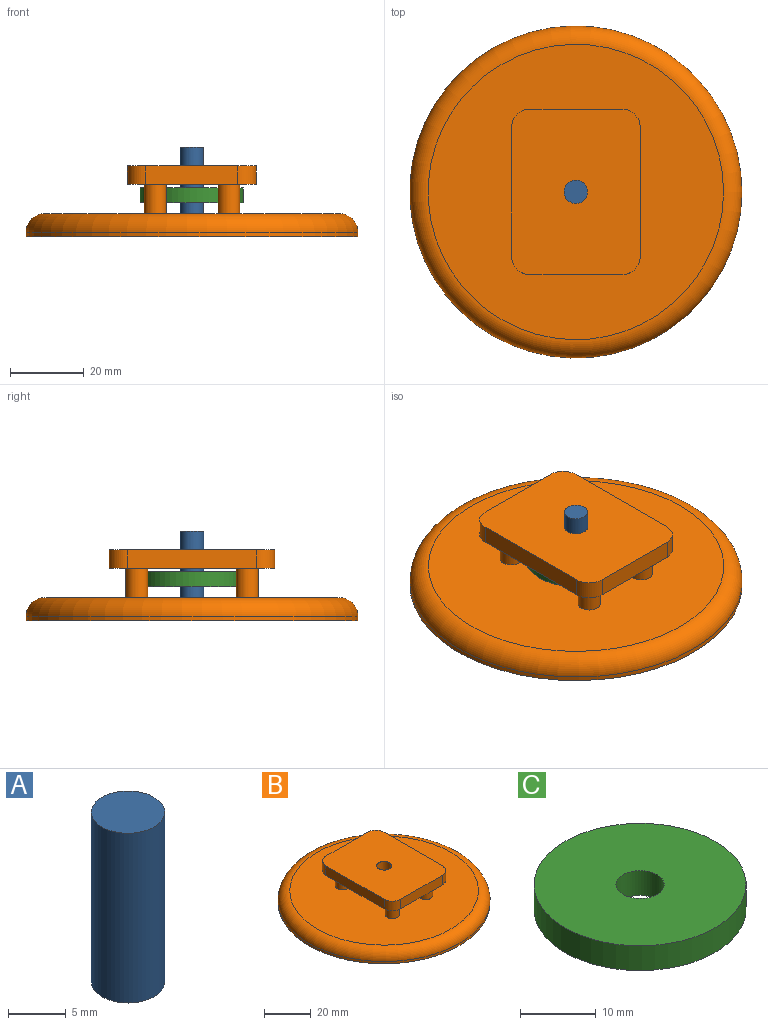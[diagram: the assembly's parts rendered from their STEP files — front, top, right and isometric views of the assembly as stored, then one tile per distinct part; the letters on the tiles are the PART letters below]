
ASSEMBLY  parts=3 mates=2
PART A: 3 faces, bbox 6.4x6.4x18 mm
  f0: cylinder r=3.17mm len=18mm, axis (0,0,-1), area 359.1mm2, adj f1,f2
  f1: plane 6.35x6.35mm, normal (0,0,-1), area 31.7mm2, adj f0
  f2: plane 6.35x6.35mm, normal (0,0,1), area 31.7mm2, adj f0
PART B: 19 faces, bbox 97.7x97.7x19.2 mm
  f0: cylinder r=45.15mm len=90.3mm, axis (0,0,-1), area 340.4mm2, adj f2,f3
  f1: plane 80.3x80.3mm, normal (0,0,1), area 4951.7mm2, adj f3,f4,f5,f6,f7
  f2: plane 90.3x90.3mm, normal (0,0,-1), area 6404.8mm2, adj f0
  f3: torus R=40.15mm, axis (0,0,1), area 2138.5mm2, adj f0,f1
  f4: cylinder r=3mm len=8mm, axis (0,0,-1), area 150.8mm2, adj f1,f14
  f5: cylinder r=3mm len=8mm, axis (0,0,-1), area 150.8mm2, adj f1,f14
  f6: cylinder r=3mm len=8mm, axis (0,0,-1), area 150.8mm2, adj f1,f14
  f7: cylinder r=3mm len=8mm, axis (0,0,-1), area 150.8mm2, adj f1,f14
  f8: plane 35x5mm, normal (-1,0,0), area 175mm2, adj f13,f14,f15,f18
  f9: plane 25x5mm, normal (0,-1,0), area 125mm2, adj f13,f14,f15,f16
  f10: plane 35x5mm, normal (1,0,0), area 175mm2, adj f13,f14,f16,f17
  f11: plane 25x5mm, normal (0,1,0), area 125mm2, adj f13,f14,f17,f18
  f12: cylinder r=3.17mm len=6.35mm, axis (0,0,-1), area 99.7mm2, adj f13,f14
  f13: plane 45x35mm, normal (0,0,1), area 1521.9mm2, adj f8,f9,f10,f11,f12,f15,f16,f17
  f14: plane 45x35mm, normal (0,0,-1), area 1408.8mm2, adj f4,f5,f6,f7,f8,f9,f10,f11
  f15: cylinder r=5mm len=5mm, axis (0,0,1), area 39.3mm2, adj f8,f9,f13,f14
  f16: cylinder r=5mm len=5mm, axis (0,0,-1), area 39.3mm2, adj f9,f10,f13,f14
  f17: cylinder r=5mm len=5mm, axis (0,0,1), area 39.3mm2, adj f10,f11,f13,f14
  f18: cylinder r=5mm len=5mm, axis (0,0,-1), area 39.3mm2, adj f8,f11,f13,f14
PART C: 4 faces, bbox 28x28x4 mm
  f0: cylinder r=3.17mm len=6.35mm, axis (0,0,-1), area 79.8mm2, adj f2,f3
  f1: cylinder r=14mm len=28mm, axis (0,0,-1), area 351.9mm2, adj f2,f3
  f2: plane 28x28mm, normal (0,0,1), area 584.1mm2, adj f0,f1
  f3: plane 28x28mm, normal (0,0,-1), area 584.1mm2, adj f0,f1
PLACE A at identity
PLACE B at identity
PLACE C at identity
MATE fastened A.f0 <-> B.f0  axis (0,0,-1) through (0,0,6.2)mm
MATE fastened C.f1 <-> A.f0  axis (0,0,-1) through (0,0,9.2)mm
